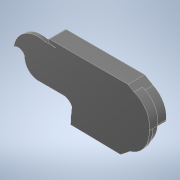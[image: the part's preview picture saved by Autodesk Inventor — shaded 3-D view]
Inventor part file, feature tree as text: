
AUTODESK INVENTOR PART (.ipt)
format: ipt  version: 2022 (Build 260153000, 153)  size: 416,256 bytes
history: native  units: in
note: dims shown in document units (in); Inventor stores cm internally (conversion verified against a paired STEP export)
features: extrude x6, sketch x6, other x1
ambient origin geometry x8: Origin, YZ Plane, XZ Plane, XY Plane, X Axis, Y Axis, Z Axis, Center Point
bodies: Body1 (feature_tree)
feature tree (13):
  other  "Sólido1"
  extrude  "Extrusión1"  Depth=0.0709in TaperAngle=0.0deg
  extrude  "Extrusión2"  Depth=0.0472in TaperAngle=0.0deg
  extrude  "Extrusión3"  Depth=0.0787in
  extrude  "Extrusión4"  Depth=0.1181in TaperAngle=0.0deg
  extrude  "Extrusión5"  Depth=0.0197in
  extrude  "Extrusión8"  Depth=0.0197in
  sketch  "Boceto1"  dims[d5=0.0472in d6=0.0in d7=0.0709in d8=0.0in]
  sketch  "Boceto2"  dims[d9=0.2362in d10=0.0in d11=0.0472in d12=0.0in]
  sketch  "Boceto3"  dims[d13=0.0472in d14=0.0in d15=0.0787in]
  sketch  "Boceto4"  dims[d16=0.0197in d23=0.1181in d24=0.0in]
  sketch  "Boceto5"  dims[d25=0.0197in d26=0.0344in]
  sketch  "Boceto13"  dims[d27=0.0197in d28=0.0344in]
